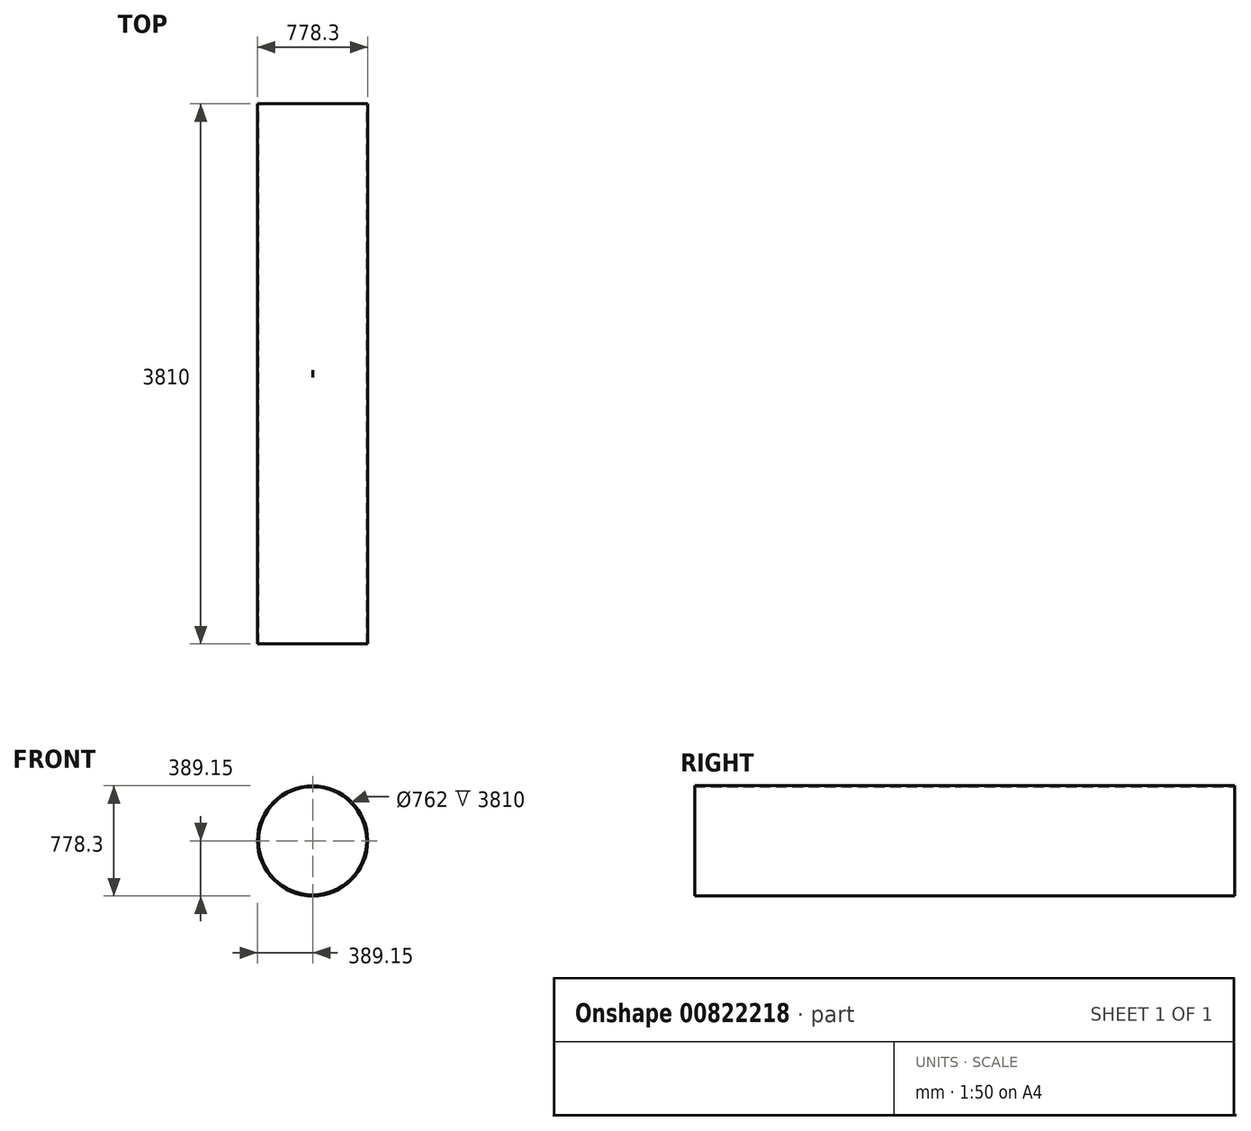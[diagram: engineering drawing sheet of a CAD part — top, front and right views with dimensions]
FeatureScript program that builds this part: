
annotation { "Feature Type Name" : "Feature", "Feature Type Description" : "" }
export const myFeature = defineFeature(function(context is Context, id is Id, definition is map)
    precondition{}
    {
        {
            var Q0;
            Q0=qCreatedBy(makeId("Front.planeOp"),FACE);
            var sketch = newSketch(context, id + "F0", { "sketchPlane" : qUnion([Q0])});
            skCircle(sketch, "E0", {"center": v(0, 0) * mm, "radius": 389.15 * mm});
            skCircle(sketch, "E1", {"center": v(0, 0) * mm, "radius": 381 * mm});
            skSolve(sketch);
        }
        {
            var Q0;
            Q0=makeQuery(id+"F0.imprint","IMPRINT",FACE,{"disambiguationData":[TD([[makeQuery(id+"F0.imprint","IMPRINT",EDGE,{"derivedFrom":sQuery(id+"F0.wireOp",EDGE,"E0")}),1.0]])]});
            extrude(context, id + "F1", {"entities" : qUnion([Q0]), "endBound" : BoundingType.SYMMETRIC, "depth" : 3810 * mm, "offsetDistance" : 25.4 * mm});
        }
        {
            var Q0;
            Q0=qCreatedBy(makeId("Top.planeOp"),FACE);
            cPlane(context, id + "F2", {"entities" : qUnion([Q0]), "cplaneType" : CPlaneType.OFFSET, "offset" : 426.72 * mm, "width" : 152.4 * mm, "height" : 152.4 * mm});
        }
        {
            var Q0;
            Q0=qCreatedBy(id+"F2.planeOp",FACE);
            var sketch = newSketch(context, id + "F3", { "sketchPlane" : qUnion([Q0])});
            skLineSegment(sketch, "E2", {"start": v(0, 25.4) * mm, "end": v(0, -25.4) * mm});
            skArc(sketch, "E3", {"start": v(0, -25.4) * mm, "mid": v(1.27, 0) * mm, "end": v(0, 25.4) * mm});
            skArc(sketch, "E4.MirrorCS", {"start": v(0, -25.4) * mm, "mid": v(-1.27, 0) * mm, "end": v(0, 25.4) * mm});
            skSolve(sketch);
        }
        {
            var Q0;
            Q0=makeQuery(id+"F3.imprint","IMPRINT",FACE,{"disambiguationData":[TD([[makeQuery(id+"F3.imprint","IMPRINT",EDGE,{"derivedFrom":sQuery(id+"F3.wireOp",EDGE,"E2")}),-1.0]])]});
            var Q1;
            Q1=makeQuery(id+"F3.imprint","IMPRINT",FACE,{"disambiguationData":[TD([[makeQuery(id+"F3.imprint","IMPRINT",EDGE,{"derivedFrom":sQuery(id+"F3.wireOp",EDGE,"E2")}),1.0]])]});
            extrude(context, id + "F4", {"entities" : qUnion([Q0, Q1]), "operationType" : NewBodyOperationType.REMOVE, "oppositeDirection" : true, "depth" : 126.24 * mm, "offsetDistance" : 25.4 * mm});
        }
    });
